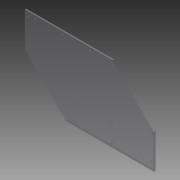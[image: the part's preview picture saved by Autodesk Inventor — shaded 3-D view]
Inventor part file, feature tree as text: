
AUTODESK INVENTOR PART (.ipt)
format: ipt  version: 2014 SP1 (Build 180222100, 222)  size: 99,328 bytes
history: native  units: in
note: dims shown in document units (in); Inventor stores cm internally (conversion verified against a paired STEP export)
features: reference x4, extrude x1, sketch x1
ambient origin geometry x8: Origin, YZ Plane, XZ Plane, XY Plane, X Axis, Y Axis, Z Axis, Center Point
bodies: Solid1 (feature_tree)
feature tree (6):
  extrude  "Extrusion1"  Depth=7.625in
  sketch  "Sketch1"  dims[d0=13.0in d1=7.625in d2=0.125in d3=0.0in]
  reference  "Reference1"
  reference  "Reference2"
  reference  "Reference3"
  reference  "Reference4"
